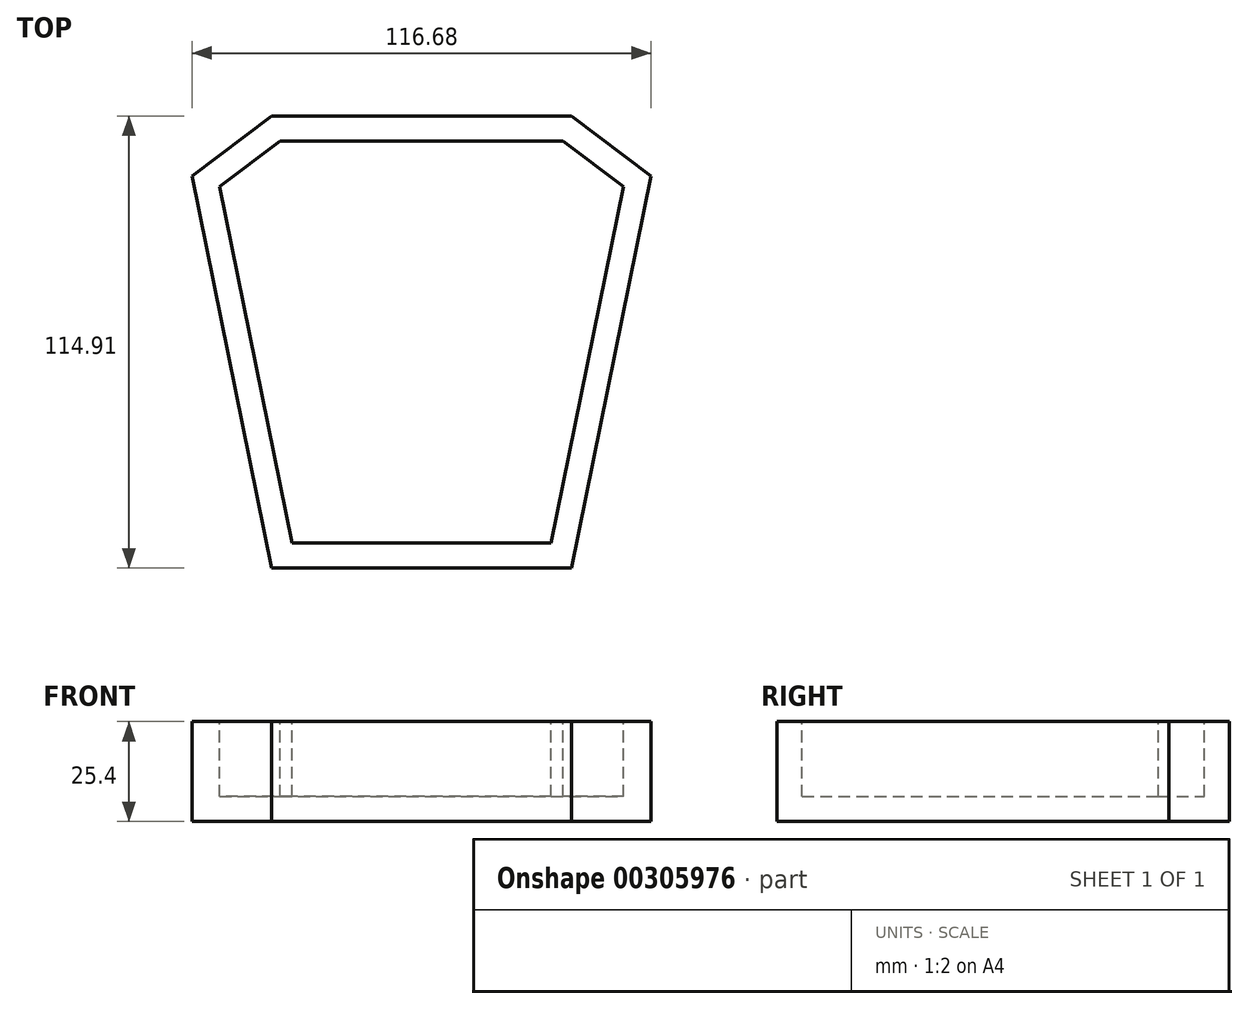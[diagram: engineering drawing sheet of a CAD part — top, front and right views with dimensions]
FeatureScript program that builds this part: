
annotation { "Feature Type Name" : "Feature", "Feature Type Description" : "" }
export const myFeature = defineFeature(function(context is Context, id is Id, definition is map)
    precondition{}
    {
        {
            var Q0;
            Q0=qCreatedBy(makeId("Top.planeOp"),FACE);
            var sketch = newSketch(context, id + "F0", { "sketchPlane" : qUnion([Q0])});
            skLineSegment(sketch, "E0", {"start": v(0, 0) * mm, "end": v(76.2, 0) * mm});
            skLineSegment(sketch, "E1", {"start": v(76.2, -114.91) * mm, "end": v(0, -114.91) * mm});
            skLineSegment(sketch, "E2", {"start": v(0, -114.91) * mm, "end": v(-20.24, -15.35) * mm});
            skLineSegment(sketch, "E3", {"start": v(-20.24, -15.35) * mm, "end": v(0, 0) * mm});
            skLineSegment(sketch, "E4", {"start": v(38.1, 0) * mm, "end": v(38.1, -114.91) * mm});
            skLineSegment(sketch, "E5.MirrorCS", {"start": v(96.44, -15.35) * mm, "end": v(76.2, 0) * mm});
            skLineSegment(sketch, "E6.MirrorCS", {"start": v(76.2, -114.91) * mm, "end": v(96.44, -15.35) * mm});
            skSolve(sketch);
        }
        {
            var Q0;
            Q0 = qSketchRegion(id + "F0", true);
            extrude(context, id + "F1", {"entities" : qUnion([Q0]), "depth" : 25.4 * mm});
        }
        {
            var Q0;
            Q0=makeQuery(id+"F1.opExtrude","CAP_FACE",FACE,{"disambiguationData":[OSD([sQuery(id+"F0.wireOp",EDGE,"E0"),sQuery(id+"F0.wireOp",EDGE,"E1"),sQuery(id+"F0.wireOp",EDGE,"E2"),sQuery(id+"F0.wireOp",EDGE,"E3"),sQuery(id+"F0.wireOp",EDGE,"E5.MirrorCS"),sQuery(id+"F0.wireOp",EDGE,"E6.MirrorCS")])],"isStart":false});
            var sketch = newSketch(context, id + "F2", { "sketchPlane" : qUnion([Q0])});
            skLineSegment(sketch, "E7.0", {"start": v(-13.22, -18) * mm, "end": v(2.14, -6.35) * mm});
            skLineSegment(sketch, "E7.1", {"start": v(89.42, -18) * mm, "end": v(74.06, -6.35) * mm});
            skLineSegment(sketch, "E7.2", {"start": v(71.01, -108.56) * mm, "end": v(89.42, -18) * mm});
            skLineSegment(sketch, "E7.3", {"start": v(2.14, -6.35) * mm, "end": v(74.06, -6.35) * mm});
            skLineSegment(sketch, "E7.4", {"start": v(71.01, -108.56) * mm, "end": v(5.19, -108.56) * mm});
            skLineSegment(sketch, "E7.5", {"start": v(5.19, -108.56) * mm, "end": v(-13.22, -18) * mm});
            skSolve(sketch);
        }
        {
            var Q0;
            Q0 = qSketchRegion(id + "F2", true);
            extrude(context, id + "F3", {"entities" : qUnion([Q0]), "operationType" : NewBodyOperationType.REMOVE, "oppositeDirection" : true, "depth" : 19.05 * mm});
        }
    });
